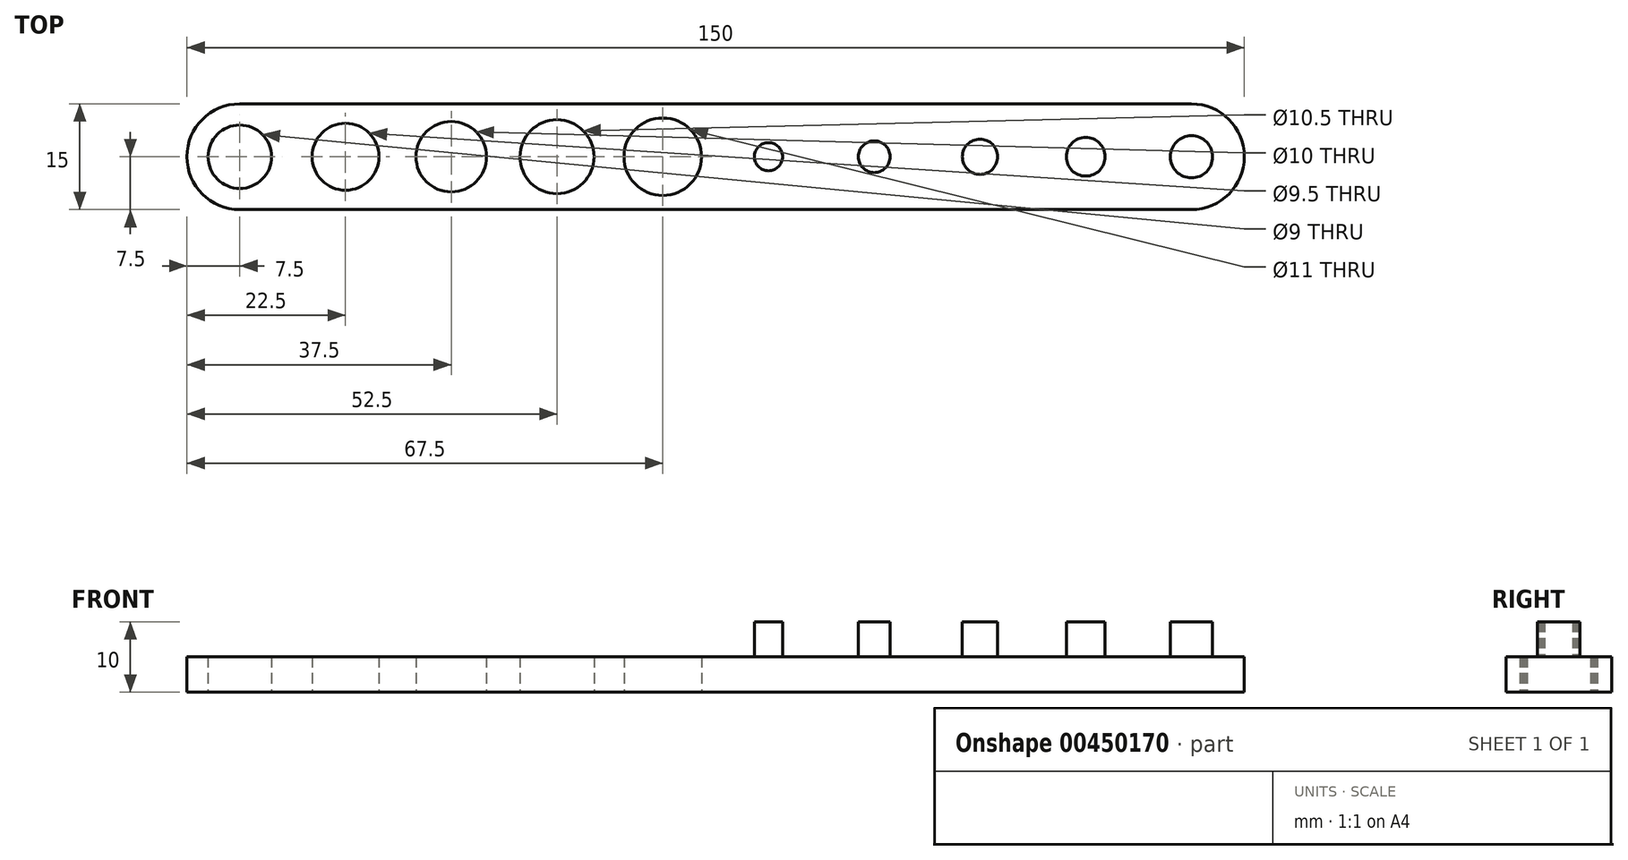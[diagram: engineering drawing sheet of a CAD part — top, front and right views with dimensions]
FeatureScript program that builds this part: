
annotation { "Feature Type Name" : "Feature", "Feature Type Description" : "" }
export const myFeature = defineFeature(function(context is Context, id is Id, definition is map)
    precondition{}
    {
        {
            var Q0;
            Q0=qCreatedBy(makeId("Top.planeOp"),FACE);
            var sketch = newSketch(context, id + "F0", { "sketchPlane" : qUnion([Q0])});
            skLineSegment(sketch, "E0.bottom", {"start": v(75, 7.5) * mm, "end": v(-75, 7.5) * mm});
            skLineSegment(sketch, "E0.top", {"start": v(75, -7.5) * mm, "end": v(-75, -7.5) * mm});
            skLineSegment(sketch, "E0.left", {"start": v(75, 7.5) * mm, "end": v(75, -7.5) * mm});
            skLineSegment(sketch, "E0.right", {"start": v(-75, 7.5) * mm, "end": v(-75, -7.5) * mm});
            skPoint(sketch, "E0.middle", {"position": v(0, 0) * mm});
            skLineSegment(sketch, "E1", {"start": v(-75, 0) * mm, "end": v(-60, 0) * mm, "construction": true});
            skPoint(sketch, "E1.endSnap0", {"position": v(-75, 0) * mm});
            skLineSegment(sketch, "E2", {"start": v(-60, 0) * mm, "end": v(-45, 0) * mm, "construction": true});
            skLineSegment(sketch, "E3", {"start": v(-45, 0) * mm, "end": v(-30, 0) * mm, "construction": true});
            skLineSegment(sketch, "E4", {"start": v(-30, 0) * mm, "end": v(-15, 0) * mm, "construction": true});
            skLineSegment(sketch, "E5", {"start": v(-15, 0) * mm, "end": v(0, 0) * mm, "construction": true});
            skCircle(sketch, "E6", {"center": v(-67.5, 0) * mm, "radius": 4.5 * mm});
            skCircle(sketch, "E7", {"center": v(-52.5, 0) * mm, "radius": 4.75 * mm});
            skCircle(sketch, "E8", {"center": v(-37.5, 0) * mm, "radius": 5 * mm});
            skCircle(sketch, "E9", {"center": v(-22.5, 0) * mm, "radius": 5.25 * mm});
            skCircle(sketch, "E10", {"center": v(-7.5, 0) * mm, "radius": 5.5 * mm});
            skSolve(sketch);
        }
        {
            var Q0;
            Q0 = qSketchRegion(id + "F0", true);
            extrude(context, id + "F1", {"entities" : qUnion([Q0]), "depth" : 5 * mm});
        }
        {
            var Q0;
            Q0=makeQuery(id+"F1.opExtrude","SWEPT_EDGE",EDGE,{"disambiguationData":[OSD([sQuery(id+"F0.wireOp",EDGE,"E0.top"),sQuery(id+"F0.wireOp",EDGE,"E0.right")])]});
            var Q1;
            Q1=makeQuery(id+"F1.opExtrude","SWEPT_EDGE",EDGE,{"disambiguationData":[OSD([sQuery(id+"F0.wireOp",EDGE,"E0.bottom"),sQuery(id+"F0.wireOp",EDGE,"E0.right")])]});
            var Q2;
            Q2=makeQuery(id+"F1.opExtrude","SWEPT_EDGE",EDGE,{"disambiguationData":[OSD([sQuery(id+"F0.wireOp",EDGE,"E0.top"),sQuery(id+"F0.wireOp",EDGE,"E0.left")])]});
            var Q3;
            Q3=makeQuery(id+"F1.opExtrude","SWEPT_EDGE",EDGE,{"disambiguationData":[OSD([sQuery(id+"F0.wireOp",EDGE,"E0.bottom"),sQuery(id+"F0.wireOp",EDGE,"E0.left")])]});
            fillet(context, id + "F2", {"entities" : qUnion([Q0, Q1, Q2, Q3]), "radius" : 7.5 * mm, "tangentPropagation" : true, "allowEdgeOverflow" : false});
        }
        {
            var Q0;
            Q0=qCreatedBy(makeId("Top.planeOp"),FACE);
            var sketch = newSketch(context, id + "F3", { "sketchPlane" : qUnion([Q0])});
            skLineSegment(sketch, "E11", {"start": v(0, 0) * mm, "end": v(15, 0) * mm, "construction": true});
            skLineSegment(sketch, "E12", {"start": v(15, 0) * mm, "end": v(30, 0) * mm, "construction": true});
            skLineSegment(sketch, "E13", {"start": v(30, 0) * mm, "end": v(45, 0) * mm, "construction": true});
            skLineSegment(sketch, "E14", {"start": v(45, 0) * mm, "end": v(60, 0) * mm, "construction": true});
            skLineSegment(sketch, "E15", {"start": v(60, 0) * mm, "end": v(75, 0) * mm, "construction": true});
            skCircle(sketch, "E16", {"center": v(67.5, 0) * mm, "radius": 3 * mm});
            skCircle(sketch, "E17", {"center": v(37.5, 0) * mm, "radius": 2.5 * mm});
            skCircle(sketch, "E18", {"center": v(52.5, 0) * mm, "radius": 2.75 * mm});
            skCircle(sketch, "E19", {"center": v(22.5, 0) * mm, "radius": 2.25 * mm});
            skCircle(sketch, "E20", {"center": v(7.5, 0) * mm, "radius": 2 * mm});
            skSolve(sketch);
        }
        {
            var Q0;
            Q0 = qSketchRegion(id + "F3", true);
            extrude(context, id + "F4", {"entities" : qUnion([Q0]), "operationType" : NewBodyOperationType.ADD, "depth" : 10 * mm});
        }
    });
